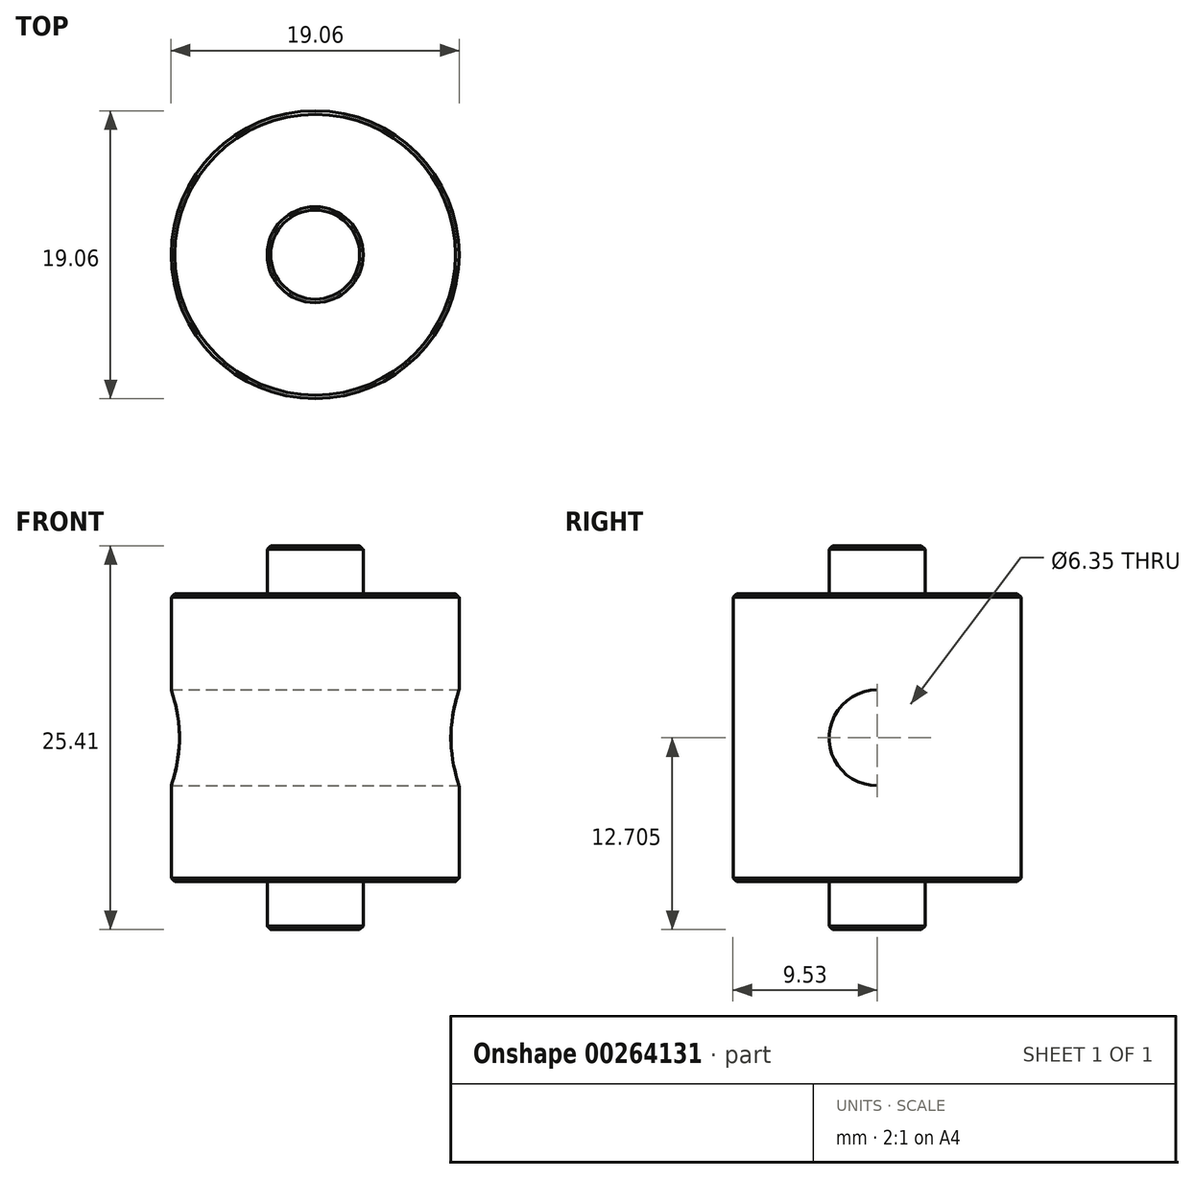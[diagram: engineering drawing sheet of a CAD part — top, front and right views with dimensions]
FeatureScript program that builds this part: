
annotation { "Feature Type Name" : "Feature", "Feature Type Description" : "" }
export const myFeature = defineFeature(function(context is Context, id is Id, definition is map)
    precondition{}
    {
        {
            var Q0;
            Q0=qCreatedBy(makeId("Top.planeOp"),FACE);
            var sketch = newSketch(context, id + "F0", { "sketchPlane" : qUnion([Q0])});
            skCircle(sketch, "E0", {"center": v(0, 0) * mm, "radius": 9.53 * mm});
            skSolve(sketch);
        }
        {
            var Q0;
            Q0 = qSketchRegion(id + "F0", true);
            extrude(context, id + "F1", {"entities" : qUnion([Q0]), "depth" : 19.05 * mm});
        }
        {
            var Q0;
            Q0=makeQuery(id+"F1.opExtrude","CAP_FACE",FACE,{"disambiguationData":[OSD([sQuery(id+"F0.wireOp",EDGE,"E0")])],"isStart":false});
            var sketch = newSketch(context, id + "F2", { "sketchPlane" : qUnion([Q0])});
            skCircle(sketch, "E1", {"center": v(0, 0) * mm, "radius": 3.18 * mm});
            skSolve(sketch);
        }
        {
            var Q0;
            Q0 = qSketchRegion(id + "F2", true);
            extrude(context, id + "F3", {"entities" : qUnion([Q0]), "operationType" : NewBodyOperationType.ADD, "depth" : 3.17 * mm});
        }
        {
            var Q0;
            Q0=makeQuery(id+"F1.opExtrude","CAP_FACE",FACE,{"disambiguationData":[OSD([sQuery(id+"F0.wireOp",EDGE,"E0")])],"isStart":true});
            var sketch = newSketch(context, id + "F4", { "sketchPlane" : qUnion([Q0])});
            skCircle(sketch, "E2", {"center": v(0, 0) * mm, "radius": 3.18 * mm});
            skSolve(sketch);
        }
        {
            var Q0;
            Q0 = qSketchRegion(id + "F4", true);
            extrude(context, id + "F5", {"entities" : qUnion([Q0]), "operationType" : NewBodyOperationType.ADD, "depth" : 3.17 * mm});
        }
        {
            var Q0;
            Q0=qCreatedBy(makeId("Right.planeOp"),FACE);
            var sketch = newSketch(context, id + "F6", { "sketchPlane" : qUnion([Q0])});
            skCircle(sketch, "E3", {"center": v(0, 9.53) * mm, "radius": 3.18 * mm});
            skSolve(sketch);
        }
        {
            var Q0;
            Q0 = qSketchRegion(id + "F6", true);
            extrude(context, id + "F7", {"entities" : qUnion([Q0]), "operationType" : NewBodyOperationType.REMOVE, "endBound" : BoundingType.THROUGH_ALL, "oppositeDirection" : true, "depth" : 25.4 * mm, "hasSecondDirection" : true, "secondDirectionOppositeDirection" : false, "secondDirectionDepth" : 25.4 * mm});
        }
        {
            var Q0;
            Q0=makeQuery(id+"F3.opExtrude","CAP_EDGE",EDGE,{"disambiguationData":[OSD([sQuery(id+"F2.wireOp",EDGE,"E1")])],"isStart":false});
            var Q1;
            Q1=makeQuery(id+"F1.opExtrude","CAP_EDGE",EDGE,{"disambiguationData":[OSD([sQuery(id+"F0.wireOp",EDGE,"E0")])],"isStart":false});
            var Q2;
            Q2=makeQuery(id+"F5.opExtrude","CAP_EDGE",EDGE,{"disambiguationData":[OSD([sQuery(id+"F4.wireOp",EDGE,"E2")])],"isStart":false});
            var Q3;
            Q3=makeQuery(id+"F1.opExtrude","CAP_EDGE",EDGE,{"disambiguationData":[OSD([sQuery(id+"F0.wireOp",EDGE,"E0")])],"isStart":true});
            chamfer(context, id + "F8", {"entities" : qUnion([Q0, Q1, Q2, Q3]), "width" : 0.23 * mm, "tangentPropagation" : true});
        }
    });
